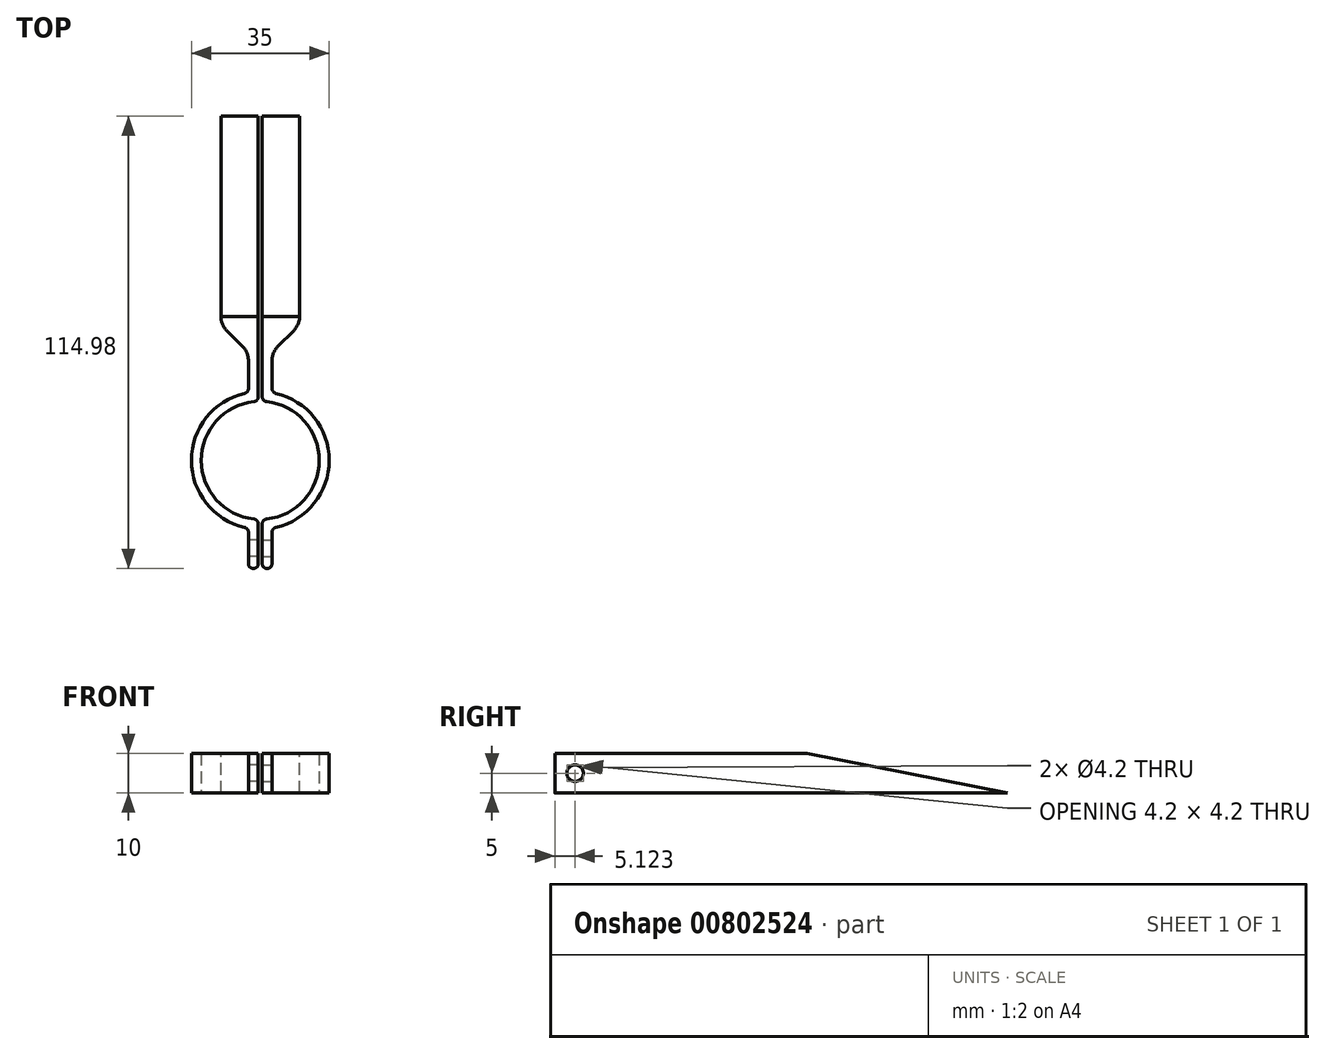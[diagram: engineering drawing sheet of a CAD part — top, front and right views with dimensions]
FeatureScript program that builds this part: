
annotation { "Feature Type Name" : "Feature", "Feature Type Description" : "" }
export const myFeature = defineFeature(function(context is Context, id is Id, definition is map)
    precondition{}
    {
        {
            var Q0;
            Q0=qCreatedBy(makeId("Top.planeOp"),FACE);
            var sketch = newSketch(context, id + "F0", { "sketchPlane" : qUnion([Q0])});
            skArc(sketch, "E0", {"start": v(-0.5, 15) * mm, "mid": v(-15, 0) * mm, "end": v(-0.5, -15) * mm});
            skArc(sketch, "E1.0", {"start": v(-0.5, 17.5) * mm, "mid": v(-17.5, 0) * mm, "end": v(-0.5, -17.5) * mm});
            skLineSegment(sketch, "E2.bottom", {"start": v(-0.5, -15) * mm, "end": v(-3, -15) * mm});
            skLineSegment(sketch, "E2.top", {"start": v(-0.5, -27.5) * mm, "end": v(-3, -27.5) * mm});
            skLineSegment(sketch, "E2.left", {"start": v(-0.5, -15) * mm, "end": v(-0.5, -27.5) * mm});
            skLineSegment(sketch, "E2.right", {"start": v(-3, -15) * mm, "end": v(-3, -27.5) * mm});
            skPoint(sketch, "E3", {"position": v(-0.5, -17.5) * mm});
            skPoint(sketch, "E4.orphan", {"position": v(0, -15) * mm});
            skLineSegment(sketch, "E5", {"start": v(0, 0) * mm, "end": v(-15, 0) * mm, "construction": true});
            skLineSegment(sketch, "E6.MirrorCS", {"start": v(-3, 15) * mm, "end": v(-3, 27.5) * mm});
            skLineSegment(sketch, "E7.MirrorCS", {"start": v(-0.5, 15) * mm, "end": v(-0.5, 27.5) * mm});
            skLineSegment(sketch, "E8.MirrorCS", {"start": v(-0.5, 27.5) * mm, "end": v(-3, 27.5) * mm});
            skLineSegment(sketch, "E9.bottom", {"start": v(-0.5, 27.5) * mm, "end": v(-10, 27.5) * mm});
            skLineSegment(sketch, "E9.top", {"start": v(-0.5, 87.5) * mm, "end": v(-10, 87.5) * mm});
            skLineSegment(sketch, "E9.left", {"start": v(-0.5, 27.5) * mm, "end": v(-0.5, 87.5) * mm});
            skLineSegment(sketch, "E9.right", {"start": v(-10, 27.5) * mm, "end": v(-10, 87.5) * mm});
            skSolve(sketch);
        }
        {
            var Q0;
            {var subQ6=sQuery(id+"F0.wireOp",EDGE,"E2.bottom");var subQ7=makeQuery(id+"F0.imprint","IMPRINT",EDGE,{"derivedFrom":subQ6});var subQ9=sQuery(id+"F0.wireOp",EDGE,"E0");var subQ16=sQuery(id+"F0.wireOp",EDGE,"E8.MirrorCS");var subQ18=makeQuery(id+"F0.imprint","IMPRINT",EDGE,{"derivedFrom":subQ16});var subQ19=sQuery(id+"F0.wireOp",EDGE,"E2.top");Q0=qUnion([makeQuery(id+"F0.imprint","IMPRINT",FACE,{"disambiguationData":[TD([[makeQuery(id+"F0.imprint","IMPRINT",EDGE,{"derivedFrom":subQ19}),-1.0]])]}),makeQuery(id+"F0.imprint","IMPRINT",FACE,{"disambiguationData":[TD([[subQ18,-1.0]])]}),makeQuery(id+"F0.imprint","IMPRINT",FACE,{"disambiguationData":[TD([[makeQuery(id+"F0.imprint","IMPRINT",EDGE,{"derivedFrom":subQ9}),-1.0]])]}),makeQuery(id+"F0.imprint","IMPRINT",FACE,{"disambiguationData":[TD([[subQ18,1.0]])]}),makeQuery(id+"F0.imprint","IMPRINT",FACE,{"disambiguationData":[TD([[subQ7,1.0]])]})]);}
            extrude(context, id + "F1", {"entities" : qUnion([Q0]), "depth" : 10 * mm, "offsetDistance" : 25 * mm});
        }
        {
            var Q0;
            Q0=makeQuery(id+"F1.opExtrude","SWEPT_EDGE",EDGE,{"disambiguationData":[OSD([sQuery(id+"F0.wireOp",EDGE,"E9.bottom"),sQuery(id+"F0.wireOp",EDGE,"E9.right")])]});
            chamfer(context, id + "F2", {"entities" : qUnion([Q0]), "width" : 7 * mm, "tangentPropagation" : true});
        }
        {
            var Q0;
            Q0=makeQuery(id+"F1.opExtrude","SWEPT_FACE",FACE,{"disambiguationData":[OSD([sQuery(id+"F0.wireOp",EDGE,"E2.right")])]});
            var sketch = newSketch(context, id + "F3", { "sketchPlane" : qUnion([Q0])});
            skCircle(sketch, "E10", {"center": v(22.37, 5) * mm, "radius": 2.1 * mm});
            skCircle(sketch, "E11.MirrorC", {"center": v(-22.37, 5) * mm, "radius": 2.1 * mm});
            skSolve(sketch);
        }
        {
            var Q0;
            Q0=makeQuery(id+"F3.imprint","IMPRINT",FACE,{"disambiguationData":[TD([[makeQuery(id+"F3.imprint","IMPRINT",EDGE,{"derivedFrom":sQuery(id+"F3.wireOp",EDGE,"E10")}),1.0]])]});
            var Q1;
            Q1=makeQuery(id+"F3.imprint","IMPRINT",FACE,{"disambiguationData":[TD([[makeQuery(id+"F3.imprint","IMPRINT",EDGE,{"derivedFrom":sQuery(id+"F3.wireOp",EDGE,"E11.MirrorC")}),-1.0]])]});
            var Q2;
            Q2=sQuery(id+"F3.wireOp",EDGE,"E10");
            extrude(context, id + "F4", {"entities" : qUnion([Q0, Q1]), "operationType" : NewBodyOperationType.REMOVE, "surfaceEntities" : qUnion([Q2]), "endBound" : BoundingType.UP_TO_NEXT, "oppositeDirection" : true, "depth" : 25 * mm, "offsetDistance" : 25 * mm});
        }
        {
            var Q0;
            {var subQ0=sQuery(id+"F0.wireOp",EDGE,"E9.right");Q0=makeQuery(id+"F2.opChamfer","BLEND_EDGE",EDGE,{"blendedFrom":[makeQuery(id+"F1.opExtrude","SWEPT_EDGE",EDGE,{"disambiguationData":[OSD([sQuery(id+"F0.wireOp",EDGE,"E9.bottom"),subQ0])]}),makeQuery(id+"F1.opExtrude","SWEPT_FACE",FACE,{"disambiguationData":[OSD([subQ0])]})],"blendedInto":[makeQuery(id+"F1.opExtrude","SWEPT_FACE",FACE,{"disambiguationData":[OSD([subQ0])]})]});}
            var Q1;
            Q1=makeQuery(id+"F2.opChamfer","BLEND_EDGE",EDGE,{"blendedFrom":[makeQuery(id+"F1.opExtrude","SWEPT_EDGE",EDGE,{"disambiguationData":[OSD([sQuery(id+"F0.wireOp",EDGE,"E9.bottom"),sQuery(id+"F0.wireOp",EDGE,"E9.right")])]}),makeQuery(id+"F1.opExtrude","SWEPT_FACE",FACE,{"disambiguationData":[OSD([sQuery(id+"F0.wireOp",EDGE,"E6.MirrorCS")])]})],"blendedInto":[makeQuery(id+"F1.opExtrude","SWEPT_FACE",FACE,{"disambiguationData":[OSD([sQuery(id+"F0.wireOp",EDGE,"E6.MirrorCS")])]})]});
            fillet(context, id + "F5", {"entities" : qUnion([Q0, Q1]), "radius" : 5 * mm, "tangentPropagation" : true, "allowEdgeOverflow" : false});
        }
        {
            var Q0;
            Q0=makeQuery(id+"F1.opExtrude","SWEPT_FACE",FACE,{"disambiguationData":[OSD([sQuery(id+"F0.wireOp",EDGE,"E9.right")])]});
            var sketch = newSketch(context, id + "F6", { "sketchPlane" : qUnion([Q0])});
            skLineSegment(sketch, "E12", {"start": v(-87.5, 0) * mm, "end": v(-36.56, 10) * mm});
            skLineSegment(sketch, "E13", {"start": v(-36.56, 10) * mm, "end": v(-87.5, 10) * mm});
            skLineSegment(sketch, "E14", {"start": v(-87.5, 10) * mm, "end": v(-87.5, 0) * mm});
            skSolve(sketch);
        }
        {
            var Q0;
            Q0=makeQuery(id+"F6.imprint","IMPRINT",FACE,{"disambiguationData":[TD([[makeQuery(id+"F6.imprint","IMPRINT",EDGE,{"derivedFrom":sQuery(id+"F6.wireOp",EDGE,"E12")}),1.0]])]});
            extrude(context, id + "F7", {"entities" : qUnion([Q0]), "operationType" : NewBodyOperationType.REMOVE, "endBound" : BoundingType.UP_TO_NEXT, "oppositeDirection" : true, "depth" : 25 * mm, "offsetDistance" : 25 * mm});
        }
        {
            var Q0;
            Q0=makeQuery(id+"F1.opExtrude","SWEPT_EDGE",EDGE,{"disambiguationData":[OSD([sQuery(id+"F0.wireOp",EDGE,"E1.0"),sQuery(id+"F0.wireOp",EDGE,"E6.MirrorCS")])]});
            var Q1;
            Q1=makeQuery(id+"F1.opExtrude","SWEPT_EDGE",EDGE,{"disambiguationData":[OSD([sQuery(id+"F0.wireOp",EDGE,"E0"),sQuery(id+"F0.wireOp",EDGE,"E7.MirrorCS")])]});
            var Q2;
            Q2=makeQuery(id+"F1.opExtrude","SWEPT_EDGE",EDGE,{"disambiguationData":[OSD([sQuery(id+"F0.wireOp",EDGE,"E0"),sQuery(id+"F0.wireOp",EDGE,"E2.bottom"),sQuery(id+"F0.wireOp",EDGE,"E2.left")])]});
            var Q3;
            Q3=makeQuery(id+"F1.opExtrude","SWEPT_EDGE",EDGE,{"disambiguationData":[OSD([sQuery(id+"F0.wireOp",EDGE,"E1.0"),sQuery(id+"F0.wireOp",EDGE,"E2.right")])]});
            var Q4;
            Q4=makeQuery(id+"F1.opExtrude","SWEPT_EDGE",EDGE,{"disambiguationData":[OSD([sQuery(id+"F0.wireOp",EDGE,"E2.top"),sQuery(id+"F0.wireOp",EDGE,"E2.right")])]});
            var Q5;
            Q5=makeQuery(id+"F1.opExtrude","SWEPT_EDGE",EDGE,{"disambiguationData":[OSD([sQuery(id+"F0.wireOp",EDGE,"E2.top"),sQuery(id+"F0.wireOp",EDGE,"E2.left")])]});
            fillet(context, id + "F8", {"entities" : qUnion([Q0, Q1, Q2, Q3, Q4, Q5]), "radius" : 1.25 * mm, "tangentPropagation" : true, "allowEdgeOverflow" : false});
        }
        {
            var Q0;
            Q0=makeQuery(id+"F1.opExtrude","SWEPT_BODY",BODY,{"disambiguationData":[OSD([sQuery(id+"F0.wireOp",EDGE,"E0"),sQuery(id+"F0.wireOp",EDGE,"E1.0"),sQuery(id+"F0.wireOp",EDGE,"E2.top"),sQuery(id+"F0.wireOp",EDGE,"E2.left"),sQuery(id+"F0.wireOp",EDGE,"E2.right"),sQuery(id+"F0.wireOp",EDGE,"E6.MirrorCS"),sQuery(id+"F0.wireOp",EDGE,"E7.MirrorCS"),sQuery(id+"F0.wireOp",EDGE,"E9.bottom"),sQuery(id+"F0.wireOp",EDGE,"E9.top"),sQuery(id+"F0.wireOp",EDGE,"E9.left"),sQuery(id+"F0.wireOp",EDGE,"E9.right")])]});
            var Q1;
            Q1=qCreatedBy(makeId("Right.planeOp"),FACE);
            mirror(context, id + "F9", {"entities" : qUnion([Q0]), "mirrorPlane" : qUnion([Q1])});
        }
    });
